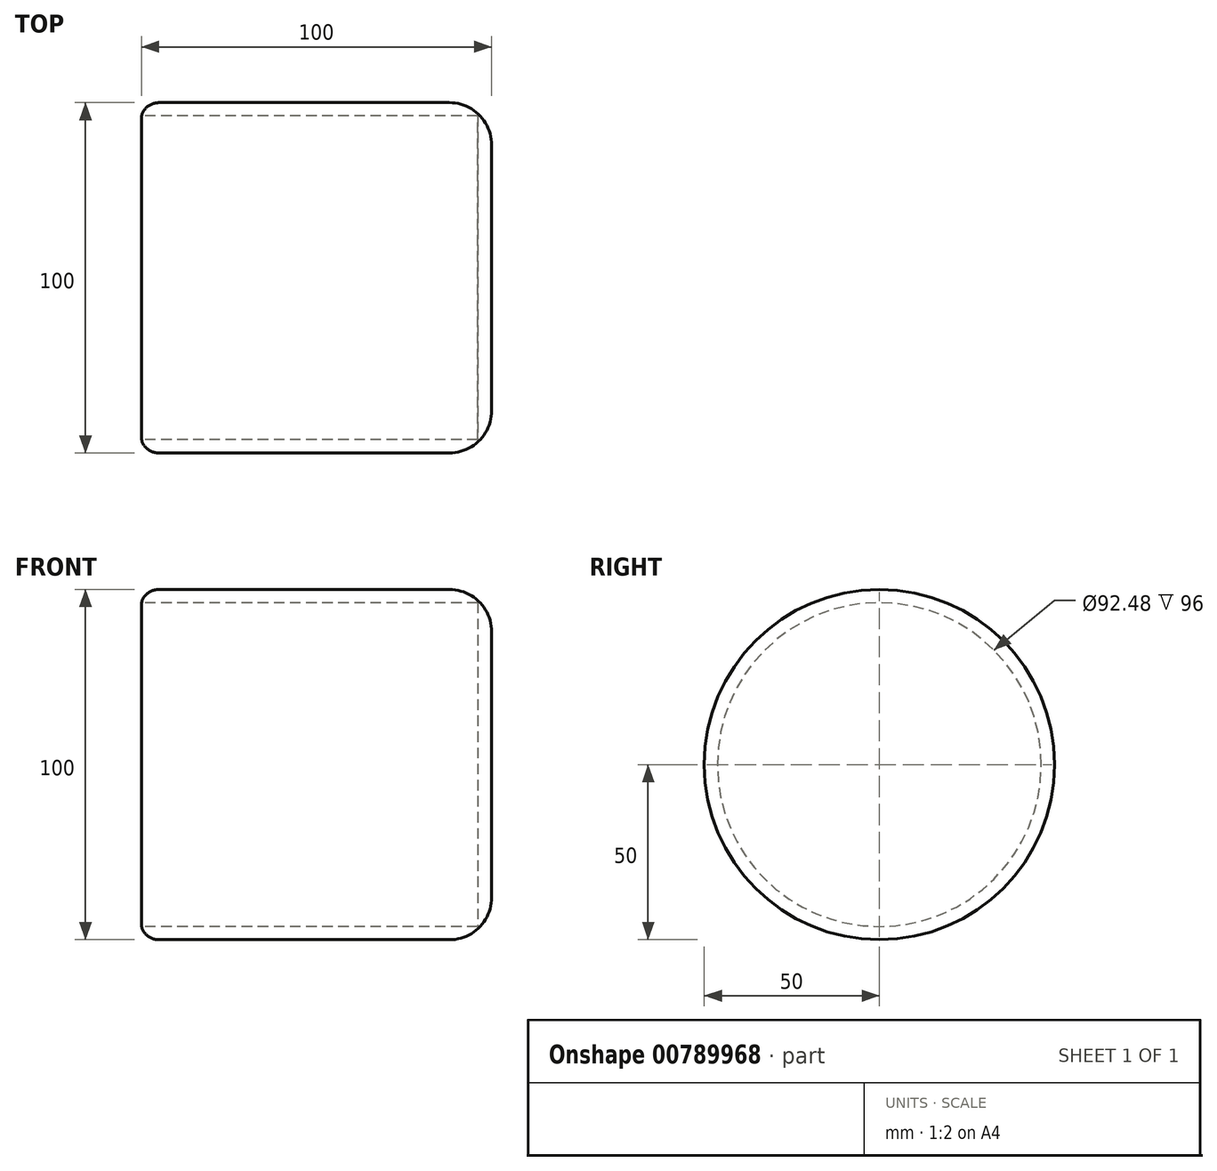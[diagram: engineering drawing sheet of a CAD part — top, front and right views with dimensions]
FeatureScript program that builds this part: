
annotation { "Feature Type Name" : "Feature", "Feature Type Description" : "" }
export const myFeature = defineFeature(function(context is Context, id is Id, definition is map)
    precondition{}
    {
        {
            var Q0;
            Q0=qCreatedBy(makeId("Right.planeOp"),FACE);
            var sketch = newSketch(context, id + "F0", { "sketchPlane" : qUnion([Q0])});
            skCircle(sketch, "E0", {"center": v(0, 0) * mm, "radius": 50 * mm});
            skSolve(sketch);
        }
        {
            var Q0;
            Q0 = qSketchRegion(id + "F0", true);
            extrude(context, id + "F1", {"entities" : qUnion([Q0]), "depth" : 100 * mm, "offsetDistance" : 25 * mm});
        }
        {
            var Q0;
            Q0=makeQuery(id+"F1.opExtrude","CAP_FACE",FACE,{"disambiguationData":[OSD([sQuery(id+"F0.wireOp",EDGE,"E0")])],"isStart":true});
            var sketch = newSketch(context, id + "F2", { "sketchPlane" : qUnion([Q0])});
            skCircle(sketch, "E1", {"center": v(0, 0) * mm, "radius": 46.24 * mm});
            skSolve(sketch);
        }
        {
            var Q0;
            Q0=makeQuery(id+"F2.imprint","IMPRINT",FACE,{"disambiguationData":[TD([[makeQuery(id+"F2.imprint","IMPRINT",EDGE,{"derivedFrom":sQuery(id+"F2.wireOp",EDGE,"E1")}),1.0]])]});
            extrude(context, id + "F3", {"entities" : qUnion([Q0]), "operationType" : NewBodyOperationType.REMOVE, "oppositeDirection" : true, "depth" : 96 * mm, "offsetDistance" : 25 * mm});
        }
        {
            var Q0;
            Q0=makeQuery(id+"F1.opExtrude","CAP_FACE",FACE,{"disambiguationData":[OSD([sQuery(id+"F0.wireOp",EDGE,"E0")])],"isStart":false});
            fillet(context, id + "F4", {"entities" : qUnion([Q0]), "radius" : 12.07 * mm, "tangentPropagation" : true, "allowEdgeOverflow" : false});
        }
        {
            var Q0;
            Q0=makeQuery(id+"F1.opExtrude","CAP_EDGE",EDGE,{"disambiguationData":[OSD([sQuery(id+"F0.wireOp",EDGE,"E0")])],"isStart":true});
            fillet(context, id + "F5", {"entities" : qUnion([Q0]), "radius" : 5 * mm, "tangentPropagation" : true, "allowEdgeOverflow" : false});
        }
    });
